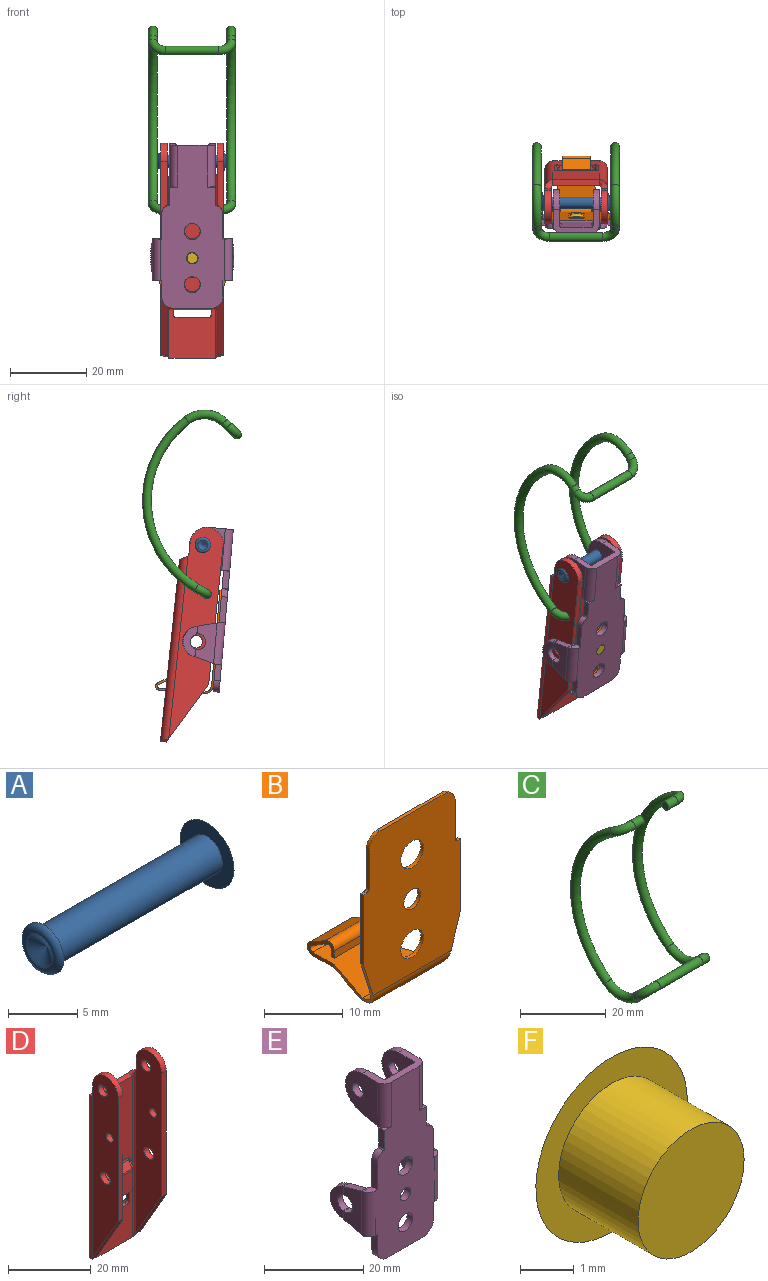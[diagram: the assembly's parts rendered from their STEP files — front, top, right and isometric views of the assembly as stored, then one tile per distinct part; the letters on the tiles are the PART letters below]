
ASSEMBLY  parts=6 mates=5
PART A: 6 faces, bbox 18x5.5x5.5 mm
  f0: cylinder r=1.55mm len=16.7mm, axis (-1,0,0), area 162.6mm2, adj f4,f5
  f1: sphere r=5mm, area 25.9mm2, adj f5
  f2: cone r=1.3mm half-angle=60deg, axis (-1,0,0), area 6.1mm2, adj f3
  f3: torus R=1.55mm, axis (-1,0,0), area 11.6mm2, adj f2,f4
  f4: plane 4.1x4.1mm, normal (1,0,0), area 5.7mm2, adj f0,f3
  f5: plane 5.5x5.5mm, normal (-1,0,0), area 16.2mm2, adj f0,f1
PART B: 35 faces, bbox 17.5x15.1x27.5 mm
  f0: cylinder r=1.5mm len=3mm, axis (0,-1,0), area 4.7mm2, adj f13,f15
  f1: cylinder r=2.05mm len=4.1mm, axis (0,-1,0), area 6.4mm2, adj f13,f15
  f2: cylinder r=2.05mm len=4.1mm, axis (0,-1,0), area 6.4mm2, adj f13,f15
  f3: cylinder r=1mm len=7.5mm, axis (-1,0,0), area 15.7mm2, adj f6,f18,f31,f33
  f4: cylinder r=0.5mm len=7.5mm, axis (-1,0,0), area 7.9mm2, adj f8,f9,f31,f33
  f5: cylinder r=1mm len=7.5mm, axis (-1,0,0), area 19.6mm2, adj f17,f18,f31,f33
  f6: plane 7.5x1.13mm, normal (0,-1,0), area 8.5mm2, adj f3,f7,f31,f33
  f7: plane 7.5x0.5mm, normal (0,0,-1), area 3.7mm2, adj f6,f8,f31,f33
  f8: plane 7.5x1.13mm, normal (0,1,0), area 8.5mm2, adj f4,f7,f31,f33
  f9: plane 7.5x2.83mm, normal (0,-0.5,-0.87), area 24.5mm2, adj f4,f10,f31,f33
  f10: cylinder r=0.5mm len=7.5mm, axis (-1,0,0), area 9.8mm2, adj f9,f11,f31,f33
  f11: plane 12.81x11.63mm, normal (0,0,1), area 108mm2, adj f10,f12,f31,f32,f33,f34
  f12: cylinder r=2mm len=14.06mm, axis (-1,0,0), area 41.7mm2, adj f11,f13,f27,f28
  f13: plane 25x17.5mm, normal (0,1,0), area 376mm2, adj f0,f1,f2,f12,f14,f19,f20,f21
  f14: plane 11.5x0.5mm, normal (0,0,1), area 5.8mm2, adj f13,f15,f29,f30
  f15: plane 25x17.5mm, normal (0,-1,0), area 376mm2, adj f0,f1,f2,f14,f16,f19,f20,f21
  f16: cylinder r=2.5mm len=14.06mm, axis (-1,0,0), area 51.3mm2, adj f15,f17,f27,f28
  f17: plane 12.5x11.63mm, normal (0,0,-1), area 107.9mm2, adj f5,f16,f27,f28,f31,f32,f33,f34
  f18: plane 7.5x2.83mm, normal (0,0.5,0.87), area 24.5mm2, adj f3,f5,f31,f33
  f19: plane 11x0.5mm, normal (1,0,0), area 5.5mm2, adj f13,f15,f21,f27
  f20: plane 11x0.5mm, normal (-1,0,0), area 5.5mm2, adj f13,f15,f25,f28
  f21: plane 0.5x0.5mm, normal (0,0,1), area 0.3mm2, adj f13,f15,f19,f22
  f22: cylinder r=0.5mm len=0.5mm, axis (0,-1,0), area 0.4mm2, adj f13,f15,f21,f23
  f23: plane 6x0.5mm, normal (1,0,0), area 3mm2, adj f13,f15,f22,f29
  f24: cylinder r=0.5mm len=0.5mm, axis (0,-1,0), area 0.4mm2, adj f13,f15,f25,f26
  f25: plane 0.5x0.5mm, normal (0,0,1), area 0.3mm2, adj f13,f15,f20,f24
  f26: plane 6x0.5mm, normal (-1,0,0), area 3mm2, adj f13,f15,f24,f30
  f27: plane 8x2.96mm, normal (0.95,0,-0.3), area 4.9mm2, adj f12,f13,f15,f16,f17,f19,f32
  f28: plane 8x2.96mm, normal (-0.95,0,-0.3), area 4.9mm2, adj f12,f13,f15,f16,f17,f20,f34
  f29: cylinder r=2mm len=2mm, axis (0,1,0), area 1.6mm2, adj f13,f14,f15,f23
  f30: cylinder r=2mm len=2mm, axis (0,1,0), area 1.6mm2, adj f13,f14,f15,f26
  f31: plane 4.83x3.63mm, normal (1,0,0), area 5.9mm2, adj f3,f4,f5,f6,f7,f8,f9,f10
  f32: plane 7.8x2.66mm, normal (0.95,0.32,0), area 4mm2, adj f11,f17,f27,f31
  f33: plane 4.83x3.63mm, normal (-1,0,0), area 5.9mm2, adj f3,f4,f5,f6,f7,f8,f9,f10
  f34: plane 7.8x2.66mm, normal (-0.95,0.32,0), area 4mm2, adj f11,f17,f28,f33
PART C: 15 faces, bbox 23.6x28.4x50.3 mm
  f0: torus R=3.2mm, axis (0,0.52,0.85), area 36.3mm2, adj f1,f8
  f1: torus R=26.6mm, axis (-1,0,0), area 375.6mm2, adj f0,f2
  f2: torus R=7.5mm, axis (-1,0,0), area 76.3mm2, adj f1,f9
  f3: torus R=3.2mm, axis (0,-0.69,-0.72), area 36.3mm2, adj f9,f10
  f4: torus R=3.2mm, axis (0,-0.69,-0.72), area 36.3mm2, adj f10,f11
  f5: torus R=7.5mm, axis (1,0,0), area 76.3mm2, adj f6,f11
  f6: torus R=26.6mm, axis (1,0,0), area 375.6mm2, adj f5,f7
  f7: torus R=3.2mm, axis (0,0.52,0.85), area 36.3mm2, adj f6,f12
  f8: cylinder r=1.15mm len=3.07mm, axis (-1,0,0), area 22.2mm2, adj f0,f14
  f9: cylinder r=1.15mm len=2.7mm, axis (0,-0.72,0.69), area 10.8mm2, adj f2,f3
  f10: cylinder r=1.15mm len=14.14mm, axis (-1,0,0), area 102.2mm2, adj f3,f4
  f11: cylinder r=1.15mm len=2.7mm, axis (0,0.72,-0.69), area 10.8mm2, adj f4,f5
  f12: cylinder r=1.15mm len=3.07mm, axis (1,0,0), area 22.2mm2, adj f7,f13
  f13: plane 2.3x2.3mm, normal (1,0,0), area 4.2mm2, adj f12
  f14: plane 2.3x2.3mm, normal (-1,0,0), area 4.2mm2, adj f8
PART D: 72 faces, bbox 16.7x12.2x57.4 mm
  f0: cylinder r=1.65mm len=3.3mm, axis (-1,0,0), area 16.6mm2, adj f17,f19
  f1: cylinder r=1.2mm len=2.4mm, axis (-1,0,0), area 12.1mm2, adj f17,f19
  f2: cylinder r=1.6mm len=3.2mm, axis (-1,0,0), area 16.1mm2, adj f17,f19
  f3: cylinder r=1.65mm len=3.3mm, axis (-1,0,0), area 16.6mm2, adj f10,f12
  f4: cylinder r=1.2mm len=2.4mm, axis (-1,0,0), area 12.1mm2, adj f10,f12
  f5: cylinder r=1.6mm len=3.2mm, axis (-1,0,0), area 16.1mm2, adj f10,f12
  f6: cylinder r=4.35mm len=8.7mm, axis (-1,0,0), area 21.9mm2, adj f7,f8,f10,f12
  f7: plane 36.52x1.6mm, normal (0,-1,0), area 58.4mm2, adj f6,f10,f11,f12
  f8: plane 2.85x1.6mm, normal (0,1,0), area 4.6mm2, adj f6,f9,f10,f12
  f9: cylinder r=2.3mm len=1.6mm, axis (-1,0,0), area 1.5mm2, adj f8,f10,f12,f32
  f10: plane 56.28x8.9mm, normal (-1,0,0), area 401.5mm2, adj f3,f4,f5,f6,f7,f8,f9,f11
  f11: plane 15.42x8.9mm, normal (0,-0.87,-0.5), area 28.5mm2, adj f7,f10,f12,f31
  f12: plane 56.28x8.9mm, normal (1,0,0), area 401.5mm2, adj f3,f4,f5,f6,f7,f8,f9,f11
  f13: cylinder r=4.35mm len=8.7mm, axis (1,0,0), area 21.9mm2, adj f14,f15,f17,f19
  f14: plane 2.85x1.6mm, normal (0,1,0), area 4.6mm2, adj f13,f17,f18,f19
  f15: plane 36.52x1.6mm, normal (0,-1,0), area 58.4mm2, adj f13,f16,f17,f19
  f16: plane 15.42x8.9mm, normal (0,-0.87,-0.5), area 28.5mm2, adj f15,f17,f19,f28
  f17: plane 56.28x8.9mm, normal (1,0,0), area 401.5mm2, adj f0,f1,f2,f13,f14,f15,f16,f18
  f18: cylinder r=2.3mm len=1.6mm, axis (1,0,0), area 1.5mm2, adj f14,f17,f19,f27
  f19: plane 56.28x8.9mm, normal (-1,0,0), area 401.5mm2, adj f0,f1,f2,f13,f14,f15,f16,f18
  f20: plane 47.95x12.5mm, normal (0,1,0), area 416.8mm2, adj f23,f25,f26,f29,f33,f42,f58,f59
  f21: plane 47.73x12.28mm, normal (0,-1,0), area 430.4mm2, adj f22,f23,f24,f25,f26,f30,f34,f38
  f22: plane 9.67x0.85mm, normal (-1,0,0), area 4mm2, adj f21,f38,f55,f58,f61,f68
  f23: plane 8.9x1.6mm, normal (0,0,1), area 13.7mm2, adj f20,f21,f68,f69,f70,f71
  f24: plane 9.67x0.85mm, normal (1,0,0), area 4mm2, adj f21,f38,f56,f59,f65,f70
  f25: plane 12.2x1.6mm, normal (0,0,1), area 19.5mm2, adj f20,f21,f27,f32
  f26: plane 12.2x1.6mm, normal (0,0,-1), area 19.5mm2, adj f20,f21,f28,f31
  f27: bspline ~2.1x2.1mm, area 4mm2, adj f18,f25,f29,f30
  f28: bspline ~2.1x2.1mm, area 3.6mm2, adj f16,f26,f29,f30
  f29: cylinder r=2.1mm len=49.01mm, axis (0,0,1), area 158mm2, adj f17,f20,f27,f28
  f30: cylinder r=0.5mm len=49.01mm, axis (0,0,1), area 37.6mm2, adj f19,f21,f27,f28
  f31: bspline ~2.1x2.1mm, area 3.6mm2, adj f11,f26,f33,f34
  f32: bspline ~2.1x2.1mm, area 4mm2, adj f9,f25,f33,f34
  f33: cylinder r=2.1mm len=49.01mm, axis (0,0,-1), area 158mm2, adj f10,f20,f31,f32
  f34: cylinder r=0.5mm len=49.01mm, axis (0,0,-1), area 37.6mm2, adj f12,f21,f31,f32
  f35: plane 8.5x5.48mm, normal (0,1,0), area 46.6mm2, adj f38,f55,f56,f57
  f36: plane 8.65x0.8mm, normal (0,0.82,-0.57), area 8.3mm2, adj f42,f57,f61,f62,f65,f66
  f37: plane 9x5.98mm, normal (0,-1,0), area 53.8mm2, adj f38,f43,f47,f48
  f38: plane 12x2.35mm, normal (0,0,-1), area 17mm2, adj f21,f22,f24,f35,f37,f40,f41,f43
  f39: plane 9x1.9mm, normal (0,-0.82,0.57), area 20.8mm2, adj f46,f47,f51,f52
  f40: plane 6.13x0.1mm, normal (1,0,0), area 0.6mm2, adj f38,f43,f45,f46
  f41: plane 6.13x0.1mm, normal (-1,0,0), area 0.6mm2, adj f38,f48,f52,f54
  f42: cylinder r=5mm len=11.5mm, axis (-1,0,0), area 30.8mm2, adj f20,f36,f63,f67
  f43: cylinder r=0.75mm len=5.98mm, axis (0,0,-1), area 7mm2, adj f37,f38,f40,f44
  f44: sphere r=0.75mm, area 0.3mm2, adj f43,f46,f47
  f45: cylinder r=0.75mm len=6.13mm, axis (0,0,-1), area 7.2mm2, adj f21,f38,f40,f49
  f46: cylinder r=0.75mm len=2.33mm, axis (0,-0.57,-0.82), area 1.8mm2, adj f39,f40,f44,f49
  f47: cylinder r=0.75mm len=9mm, axis (-1,0,0), area 4.1mm2, adj f37,f39,f44,f50
  f48: cylinder r=0.75mm len=5.98mm, axis (0,0,1), area 7mm2, adj f37,f38,f41,f50
  f49: bspline ~2.62x1.5mm, area 2.2mm2, adj f21,f45,f46,f51
  f50: sphere r=0.75mm, area 0.5mm2, adj f47,f48,f52
  f51: cylinder r=0.75mm len=9mm, axis (1,0,0), area 4.1mm2, adj f21,f39,f49,f53
  f52: cylinder r=0.75mm len=2.33mm, axis (0,0.57,0.82), area 1.8mm2, adj f39,f41,f50,f53
  f53: bspline ~2.62x1.5mm, area 2.2mm2, adj f21,f51,f52,f54
  f54: cylinder r=0.75mm len=6.13mm, axis (0,0,1), area 7.2mm2, adj f21,f38,f41,f53
  f55: cylinder r=0.75mm len=5.48mm, axis (0,0,1), area 6.5mm2, adj f22,f35,f38,f60
  f56: cylinder r=0.75mm len=5.48mm, axis (0,0,1), area 6.5mm2, adj f24,f35,f38,f64
  f57: cylinder r=0.75mm len=8.5mm, axis (1,0,0), area 3.9mm2, adj f35,f36,f60,f64
  f58: cylinder r=0.75mm len=13.63mm, axis (0,0,-1), area 13.6mm2, adj f20,f22,f62,f63,f69
  f59: cylinder r=0.75mm len=13.63mm, axis (0,0,1), area 13.6mm2, adj f20,f24,f66,f67,f71
  f60: sphere r=0.75mm, area 0.3mm2, adj f55,f57,f61
  f61: cylinder r=0.75mm len=0.75mm, axis (0,-0.57,-0.82), area 0.2mm2, adj f22,f36,f60,f62
  f62: bspline ~1.09x0.84mm, area 0.8mm2, adj f36,f58,f61,f63
  f63: bspline ~3.3x1.43mm, area 1.1mm2, adj f42,f58,f62
  f64: sphere r=0.75mm, area 0.5mm2, adj f56,f57,f65
  f65: cylinder r=0.75mm len=0.75mm, axis (0,0.57,0.82), area 0.2mm2, adj f24,f36,f64,f66
  f66: bspline ~1.09x0.84mm, area 0.8mm2, adj f36,f59,f65,f67
  f67: bspline ~3.3x1.43mm, area 1.1mm2, adj f42,f59,f66
  f68: cylinder r=0.75mm len=0.85mm, axis (0,-1,0), area 1mm2, adj f21,f22,f23,f69
  f69: torus R=1.5mm, axis (0,0,-1), area 1.2mm2, adj f20,f23,f58,f68
  f70: cylinder r=0.75mm len=0.85mm, axis (0,-1,0), area 1mm2, adj f21,f23,f24,f71
  f71: torus R=1.5mm, axis (0,0,-1), area 1.2mm2, adj f20,f23,f59,f70
PART E: 87 faces, bbox 21.9x11.1x42.9 mm
  f0: cylinder r=2.1mm len=4.2mm, axis (0,-1,0), area 21.1mm2, adj f36,f37
  f1: cylinder r=1.5mm len=3mm, axis (0,-1,0), area 15.1mm2, adj f36,f37
  f2: cylinder r=2.1mm len=4.2mm, axis (0,-1,0), area 21.1mm2, adj f36,f37
  f3: cylinder r=2.05mm len=4.1mm, axis (1,0,0), area 11.5mm2, adj f33,f35,f80,f83
  f4: cylinder r=2.05mm len=4.1mm, axis (1,0,0), area 11.5mm2, adj f29,f31,f72,f75
  f5: cylinder r=4.76mm len=9.36mm, axis (1,0,0), area 21.9mm2, adj f23,f25,f26,f27
  f6: cylinder r=1.55mm len=3.1mm, axis (1,0,0), area 15.6mm2, adj f25,f27
  f7: cylinder r=1.55mm len=3.1mm, axis (1,0,0), area 15.6mm2, adj f22,f24
  f8: cylinder r=4mm len=7.73mm, axis (0.99,-0.12,0), area 16.8mm2, adj f10,f11,f13,f14
  f9: cylinder r=4mm len=7.73mm, axis (-0.99,-0.12,0), area 16.8mm2, adj f15,f16,f17,f19
  f10: plane 1.65x0.68mm, normal (0.03,0.26,-0.97), area 0.8mm2, adj f8,f11,f13,f79
  f11: plane 7.99x3.44mm, normal (-0.99,0.12,0), area 16.4mm2, adj f8,f10,f12,f14,f81,f85
  f12: cylinder r=2.05mm len=3.96mm, axis (0.99,-0.12,0), area 8.6mm2, adj f11,f13,f80,f83
  f13: plane 7.99x3.44mm, normal (0.99,-0.12,0), area 16.4mm2, adj f8,f10,f12,f14,f82,f86
  f14: plane 1.65x0.68mm, normal (0.03,0.26,0.97), area 0.8mm2, adj f8,f11,f13,f84
  f15: plane 7.99x3.44mm, normal (0.99,0.12,0), area 16.4mm2, adj f9,f16,f18,f19,f73,f77
  f16: plane 1.65x0.68mm, normal (-0.03,0.26,-0.97), area 0.8mm2, adj f9,f15,f17,f76
  f17: plane 7.99x3.44mm, normal (-0.99,-0.12,0), area 16.4mm2, adj f9,f16,f18,f19,f74,f78
  f18: cylinder r=2.05mm len=3.96mm, axis (0.99,0.12,0), area 8.6mm2, adj f15,f17,f72,f75
  f19: plane 1.65x0.68mm, normal (-0.03,0.26,0.97), area 0.8mm2, adj f9,f15,f17,f71
  f20: cylinder r=4.76mm len=9.36mm, axis (-1,0,0), area 21.9mm2, adj f21,f22,f23,f24
  f21: plane 5.48x1.6mm, normal (0,0.26,-0.97), area 9.1mm2, adj f20,f22,f24,f68
  f22: plane 10.83x9.01mm, normal (-1,0,0), area 71.8mm2, adj f7,f20,f21,f23,f69
  f23: plane 12x6.35mm, normal (0,0,1), area 32.6mm2, adj f5,f20,f22,f24,f25,f27,f36,f37
  f24: plane 10.83x9.01mm, normal (1,0,0), area 71.8mm2, adj f7,f20,f21,f23,f70
  f25: plane 10.83x9.01mm, normal (1,0,0), area 71.8mm2, adj f5,f6,f23,f26,f66
  f26: plane 5.48x1.6mm, normal (0,0.26,-0.97), area 9.1mm2, adj f5,f25,f27,f65
  f27: plane 10.83x9.01mm, normal (-1,0,0), area 71.8mm2, adj f5,f6,f23,f26,f67
  f28: plane 4.98x1.6mm, normal (0,0.26,-0.97), area 8.2mm2, adj f29,f31,f62,f76
  f29: plane 10.73x4.98mm, normal (-1,0,0), area 38.7mm2, adj f4,f28,f30,f63,f74,f78
  f30: plane 4.98x1.6mm, normal (0,0.26,0.97), area 8.2mm2, adj f29,f31,f61,f71
  f31: plane 10.73x4.98mm, normal (1,0,0), area 38.7mm2, adj f4,f28,f30,f64,f73,f77
  f32: plane 4.98x1.6mm, normal (0,0.26,0.97), area 8.2mm2, adj f33,f35,f58,f84
  f33: plane 10.73x4.98mm, normal (1,0,0), area 38.7mm2, adj f3,f32,f34,f59,f82,f86
  f34: plane 4.98x1.6mm, normal (0,0.26,-0.97), area 8.2mm2, adj f33,f35,f57,f79
  f35: plane 10.73x4.98mm, normal (-1,0,0), area 38.7mm2, adj f3,f32,f34,f60,f81,f85
  f36: plane 42.86x16.8mm, normal (0,-1,0), area 544.9mm2, adj f0,f1,f2,f23,f38,f39,f40,f41
  f37: plane 42.86x16.8mm, normal (0,1,0), area 544.9mm2, adj f0,f1,f2,f23,f38,f39,f40,f41
  f38: plane 2.1x1.6mm, normal (0,0,1), area 3.4mm2, adj f36,f37,f56,f68
  f39: plane 2.1x1.6mm, normal (0,0,1), area 3.4mm2, adj f36,f37,f40,f65
  f40: plane 4.63x1.6mm, normal (1,0,0), area 7.4mm2, adj f36,f37,f39,f41
  f41: cylinder r=0.25mm len=1.6mm, axis (0,-1,0), area 0.6mm2, adj f36,f37,f40,f42
  f42: cylinder r=2mm len=1.99mm, axis (0,-1,0), area 4.7mm2, adj f36,f37,f41,f43
  f43: plane 6.79x1.6mm, normal (1,0,0), area 10.9mm2, adj f36,f37,f42,f44
  f44: plane 2.35x1.91mm, normal (0,0,1), area 3.1mm2, adj f36,f37,f43,f58,f59,f60
  f45: plane 2.35x1.91mm, normal (0,0,-1), area 3.1mm2, adj f36,f37,f46,f57,f59,f60
  f46: plane 4.24x1.6mm, normal (1,0,0), area 6.8mm2, adj f36,f37,f45,f47
  f47: cylinder r=3mm len=3mm, axis (0,-1,0), area 7.5mm2, adj f36,f37,f46,f48
  f48: plane 10x1.6mm, normal (0,0,-1), area 16mm2, adj f36,f37,f47,f49
  f49: cylinder r=3mm len=3mm, axis (0,-1,0), area 7.5mm2, adj f36,f37,f48,f50
  f50: plane 4.24x1.6mm, normal (-1,0,0), area 6.8mm2, adj f36,f37,f49,f51
  f51: plane 2.35x1.91mm, normal (0,0,-1), area 3.1mm2, adj f36,f37,f50,f62,f63,f64
  f52: plane 2.35x1.91mm, normal (0,0,1), area 3.1mm2, adj f36,f37,f53,f61,f63,f64
  f53: plane 6.79x1.6mm, normal (-1,0,0), area 10.9mm2, adj f36,f37,f52,f54
  f54: cylinder r=2mm len=1.99mm, axis (0,-1,0), area 4.7mm2, adj f36,f37,f53,f55
  f55: cylinder r=0.25mm len=1.6mm, axis (0,-1,0), area 0.6mm2, adj f36,f37,f54,f56
  f56: plane 4.63x1.6mm, normal (-1,0,0), area 7.4mm2, adj f36,f37,f38,f55
  f57: bspline ~1.65x0.79mm, area 0.8mm2, adj f34,f45,f59,f60
  f58: bspline ~1.65x0.79mm, area 0.8mm2, adj f32,f44,f59,f60
  f59: cylinder r=2.1mm len=11mm, axis (0,0,-1), area 36.2mm2, adj f33,f36,f44,f45,f57,f58
  f60: cylinder r=0.5mm len=11mm, axis (0,0,-1), area 8.6mm2, adj f35,f37,f44,f45,f57,f58
  f61: bspline ~1.65x0.79mm, area 0.8mm2, adj f30,f52,f63,f64
  f62: bspline ~1.65x0.79mm, area 0.8mm2, adj f28,f51,f63,f64
  f63: cylinder r=2.1mm len=11mm, axis (0,0,1), area 36.2mm2, adj f29,f36,f51,f52,f61,f62
  f64: cylinder r=0.5mm len=11mm, axis (0,0,1), area 8.6mm2, adj f31,f37,f51,f52,f61,f62
  f65: bspline ~2.12x2.12mm, area 3.3mm2, adj f26,f39,f66,f67
  f66: cylinder r=2.1mm len=10.97mm, axis (0,0,-1), area 36mm2, adj f23,f25,f36,f65
  f67: cylinder r=0.5mm len=10.97mm, axis (0,0,-1), area 8.6mm2, adj f23,f27,f37,f65
  f68: bspline ~2.12x2.12mm, area 3.3mm2, adj f21,f38,f69,f70
  f69: cylinder r=2.1mm len=10.97mm, axis (0,0,1), area 36mm2, adj f22,f23,f36,f68
  f70: cylinder r=0.5mm len=10.97mm, axis (0,0,1), area 8.6mm2, adj f23,f24,f37,f68
  f71: bspline ~1.6x0.26mm, area 0.3mm2, adj f19,f30,f73,f74
  f72: bspline ~1.6x0.26mm, area 0.3mm2, adj f4,f18,f73,f74
  f73: cylinder r=2.1mm len=2.06mm, axis (0,0,-1), area 0.5mm2, adj f15,f31,f71,f72
  f74: cylinder r=0.5mm len=2.06mm, axis (0,0,-1), area 0.1mm2, adj f17,f29,f71,f72
  f75: bspline ~1.6x0.26mm, area 0.3mm2, adj f4,f18,f77,f78
  f76: bspline ~1.6x0.26mm, area 0.3mm2, adj f16,f28,f77,f78
  f77: cylinder r=2.1mm len=2.06mm, axis (0,0,-1), area 0.5mm2, adj f15,f31,f75,f76
  f78: cylinder r=0.5mm len=2.06mm, axis (0,0,-1), area 0.1mm2, adj f17,f29,f75,f76
  f79: bspline ~1.6x0.26mm, area 0.3mm2, adj f10,f34,f81,f82
  f80: bspline ~1.6x0.26mm, area 0.3mm2, adj f3,f12,f81,f82
  f81: cylinder r=2.1mm len=2.06mm, axis (0,0,1), area 0.5mm2, adj f11,f35,f79,f80
  f82: cylinder r=0.5mm len=2.06mm, axis (0,0,1), area 0.1mm2, adj f13,f33,f79,f80
  f83: bspline ~1.6x0.26mm, area 0.3mm2, adj f3,f12,f85,f86
  f84: bspline ~1.6x0.26mm, area 0.3mm2, adj f14,f32,f85,f86
  f85: cylinder r=2.1mm len=2.06mm, axis (0,0,1), area 0.5mm2, adj f11,f35,f83,f84
  f86: cylinder r=0.5mm len=2.06mm, axis (0,0,1), area 0.1mm2, adj f13,f33,f83,f84
PART F: 4 faces, bbox 4x2.6x4 mm
  f0: cylinder r=1.4mm len=2.8mm, axis (0,-1,0), area 18.5mm2, adj f2,f3
  f1: sphere r=4mm, area 13.5mm2, adj f2
  f2: plane 4x4mm, normal (0,-1,0), area 6.4mm2, adj f0,f1
  f3: plane 2.8x2.8mm, normal (0,-1,0), area 6.2mm2, adj f0
PLACE A rot(axis=(1,0,0),15.4deg) t=(-1.07,15.06,14.38)mm
PLACE B rot(axis=(1,0,0),5deg) t=(-1.23,10.56,2.55)mm
PLACE C rot(axis=(0,-1,0),180deg) t=(-1.32,14.13,12.96)mm
PLACE D rot(axis=(1,0,0),6deg) t=(-1.27,17.86,-10.68)mm
PLACE E rot(axis=(1,0,0),5deg) t=(-1.23,8.92,-2.89)mm fixed
PLACE F rot(axis=(1,0,0),5deg) t=(-1.23,9.64,-11.08)mm
MATE revolute E.f6 <-> D.f2  axis (-1,0,0) through (-7.23,15.06,14.38)mm
MATE fastened F.f0 <-> B.f0  axis (0,-1,-0.09) through (-1.23,11.73,-10.9)mm
MATE revolute C.f8 <-> D.f1  axis (1,0,0) through (-6.85,14.04,1.51)mm
MATE revolute A.f0 <-> D.f2  axis (-1,0,0) through (6.93,15.06,14.38)mm
MATE fastened E.f0 <-> B.f1  axis (0,1,0.09) through (-1.23,11.84,-17.92)mm
